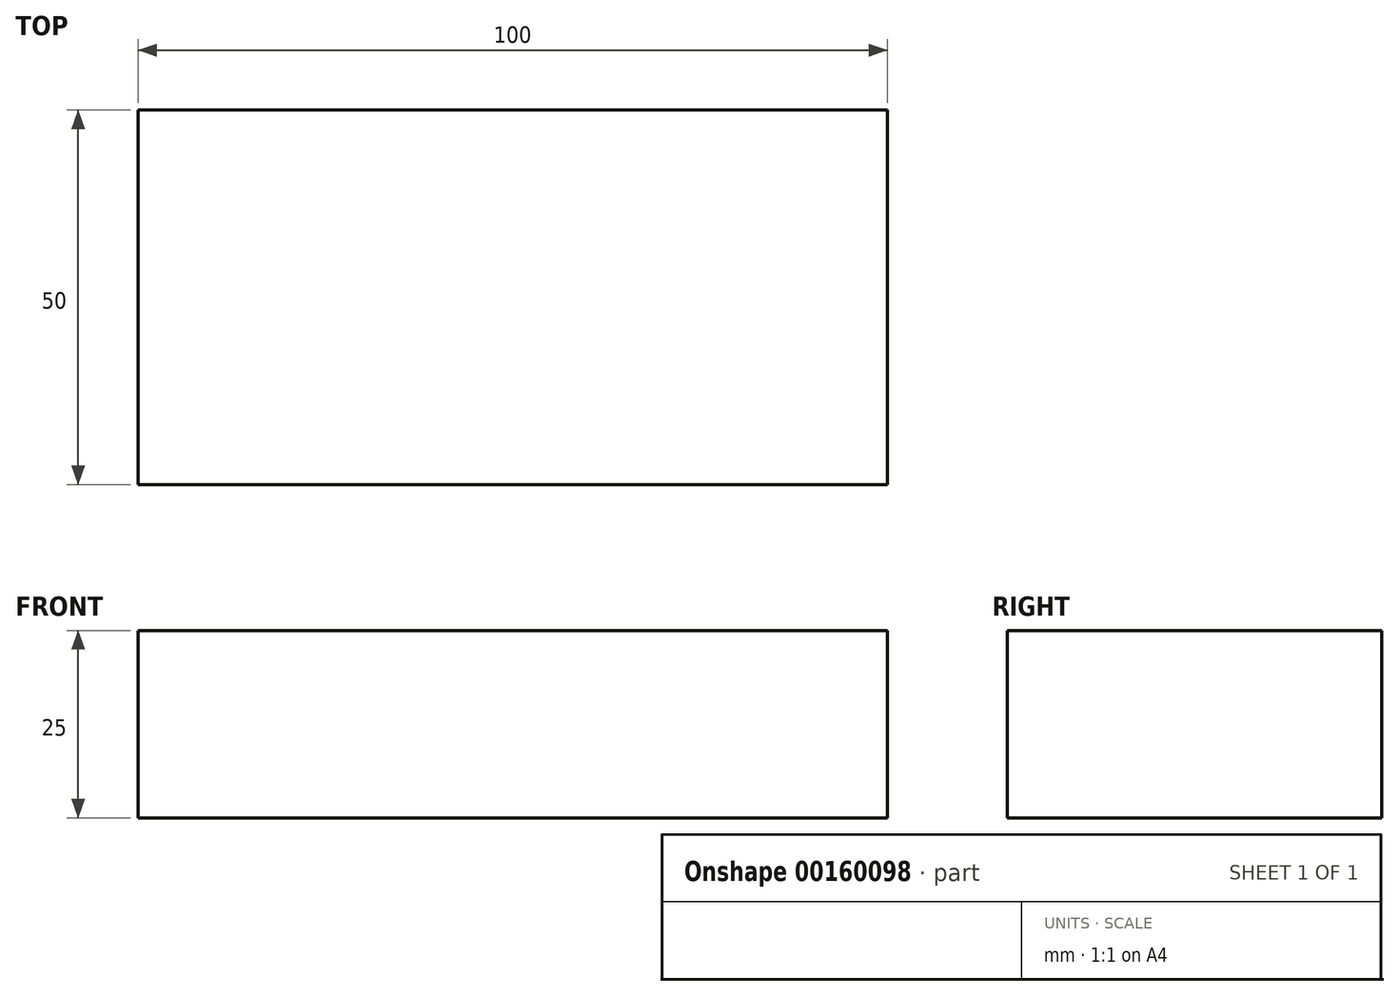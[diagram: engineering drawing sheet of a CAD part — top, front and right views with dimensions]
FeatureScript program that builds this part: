
annotation { "Feature Type Name" : "Feature", "Feature Type Description" : "" }
export const myFeature = defineFeature(function(context is Context, id is Id, definition is map)
    precondition{}
    {
        {
            var Q0;
            Q0=qCreatedBy(makeId("Front.planeOp"),FACE);
            var sketch = newSketch(context, id + "F0", { "sketchPlane" : qUnion([Q0])});
            skLineSegment(sketch, "E0.bottom", {"start": v(0, 29.22) * mm, "end": v(100, 29.22) * mm});
            skLineSegment(sketch, "E0.top", {"start": v(0, 4.22) * mm, "end": v(100, 4.22) * mm});
            skLineSegment(sketch, "E0.left", {"start": v(0, 29.22) * mm, "end": v(0, 4.22) * mm});
            skLineSegment(sketch, "E0.right", {"start": v(100, 29.22) * mm, "end": v(100, 4.22) * mm});
            skSolve(sketch);
        }
        {
            var Q0;
            Q0 = qSketchRegion(id + "F0", true);
            extrude(context, id + "F1", {"entities" : qUnion([Q0]), "depth" : 50 * mm});
        }
    });
